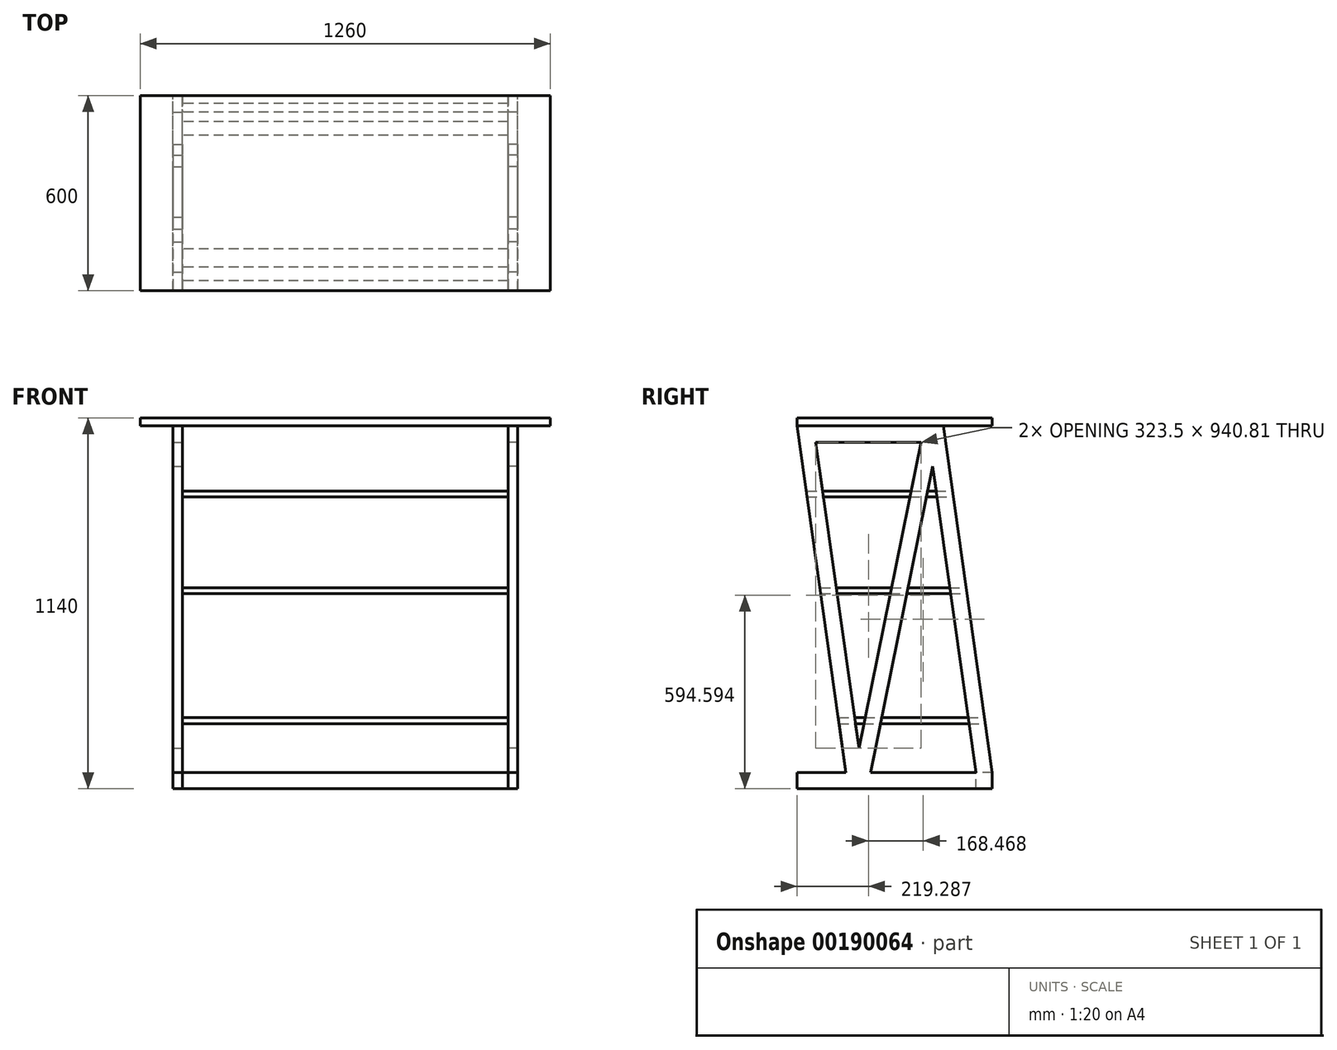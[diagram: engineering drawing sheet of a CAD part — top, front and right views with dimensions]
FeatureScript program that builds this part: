
annotation { "Feature Type Name" : "Feature", "Feature Type Description" : "" }
export const myFeature = defineFeature(function(context is Context, id is Id, definition is map)
    precondition{}
    {
        {
            var Q0;
            Q0=qCreatedBy(makeId("Right.planeOp"),FACE);
            cPlane(context, id + "F0", {"entities" : qUnion([Q0]), "cplaneType" : CPlaneType.OFFSET, "offset" : 500 * mm, "width" : 150 * mm, "height" : 150 * mm});
        }
        {
            var Q0;
            Q0=qCreatedBy(id+"F0.planeOp",FACE);
            var sketch = newSketch(context, id + "F1", { "sketchPlane" : qUnion([Q0])});
            skLineSegment(sketch, "E0", {"start": v(-600, 0) * mm, "end": v(0, 0) * mm});
            skLineSegment(sketch, "E1", {"start": v(-150, 1115) * mm, "end": v(-600, 1115) * mm});
            skLineSegment(sketch, "E2", {"start": v(-600, 1115) * mm, "end": v(-450, 50) * mm});
            skLineSegment(sketch, "E3", {"start": v(-542.46, 1065) * mm, "end": v(-409.96, 124.19) * mm});
            skLineSegment(sketch, "E4", {"start": v(-374, 50) * mm, "end": v(-50.5, 50) * mm});
            skLineSegment(sketch, "E5", {"start": v(-600, 1115) * mm, "end": v(-600, 0) * mm, "construction": true});
            skLineSegment(sketch, "E6", {"start": v(-600, 1115) * mm, "end": v(-600, 1115) * mm});
            skLineSegment(sketch, "E7", {"start": v(-600, 0) * mm, "end": v(-600, 50) * mm});
            skLineSegment(sketch, "E8", {"start": v(-600, 50) * mm, "end": v(-450, 50) * mm});
            skLineSegment(sketch, "E9", {"start": v(-150, 1115) * mm, "end": v(0, 1115) * mm, "construction": true});
            skLineSegment(sketch, "E10", {"start": v(-150, 1115) * mm, "end": v(0, 50) * mm});
            skLineSegment(sketch, "E11", {"start": v(0, 50) * mm, "end": v(0, 0) * mm});
            skLineSegment(sketch, "E12", {"start": v(0, 1115) * mm, "end": v(0, 50) * mm, "construction": true});
            skLineSegment(sketch, "E13", {"start": v(-542.46, 1065) * mm, "end": v(-218.96, 1065) * mm});
            skLineSegment(sketch, "E14", {"start": v(-183, 990.81) * mm, "end": v(-50.5, 50) * mm});
            skLineSegment(sketch, "E15", {"start": v(-193.45, 1065) * mm, "end": v(-399.5, 50) * mm, "construction": true});
            skLineSegment(sketch, "E16.0", {"start": v(-183, 990.81) * mm, "end": v(-374, 50) * mm});
            skLineSegment(sketch, "E17.0", {"start": v(-218.96, 1065) * mm, "end": v(-409.96, 124.19) * mm});
            skSolve(sketch);
        }
        {
            var Q0;
            Q0=qSketchRegion(id+"F1",true);
            extrude(context, id + "F2", {"entities" : qUnion([Q0]), "depth" : 30 * mm});
        }
        {
            var Q0;
            Q0=qCreatedBy(makeId("Front.planeOp"),FACE);
            var sketch = newSketch(context, id + "F3", { "sketchPlane" : qUnion([Q0])});
            skLineSegment(sketch, "E18.bottom", {"start": v(0, 1140) * mm, "end": v(630, 1140) * mm});
            skLineSegment(sketch, "E18.top", {"start": v(0, 1115) * mm, "end": v(630, 1115) * mm});
            skLineSegment(sketch, "E18.left", {"start": v(0, 1140) * mm, "end": v(0, 1115) * mm});
            skLineSegment(sketch, "E18.right", {"start": v(630, 1140) * mm, "end": v(630, 1115) * mm});
            skSolve(sketch);
        }
        {
            var Q0;
            Q0=qSketchRegion(id+"F3",true);
            extrude(context, id + "F4", {"entities" : qUnion([Q0]), "operationType" : NewBodyOperationType.ADD, "depth" : 600 * mm});
        }
        {
            var Q0;
            Q0=qCreatedBy(makeId("Right.planeOp"),FACE);
            var sketch = newSketch(context, id + "F5", { "sketchPlane" : qUnion([Q0])});
            skLineSegment(sketch, "E19.bottom", {"start": v(-569.3, 915) * mm, "end": v(-121.83, 915) * mm});
            skLineSegment(sketch, "E19.top", {"start": v(-569.3, 897) * mm, "end": v(-121.83, 897) * mm});
            skLineSegment(sketch, "E19.left", {"start": v(-569.3, 915) * mm, "end": v(-569.3, 897) * mm});
            skLineSegment(sketch, "E19.right", {"start": v(-121.83, 915) * mm, "end": v(-121.83, 897) * mm});
            skLineSegment(sketch, "E20.bottom", {"start": v(-527.46, 618) * mm, "end": v(-80, 618) * mm});
            skLineSegment(sketch, "E20.top", {"start": v(-527.46, 600) * mm, "end": v(-80, 600) * mm});
            skLineSegment(sketch, "E20.left", {"start": v(-527.46, 618) * mm, "end": v(-527.46, 600) * mm});
            skLineSegment(sketch, "E20.right", {"start": v(-80, 618) * mm, "end": v(-80, 600) * mm});
            skLineSegment(sketch, "E21.bottom", {"start": v(-471.13, 218) * mm, "end": v(-23.66, 218) * mm});
            skLineSegment(sketch, "E21.top", {"start": v(-471.13, 200) * mm, "end": v(-23.66, 200) * mm});
            skLineSegment(sketch, "E21.left", {"start": v(-471.13, 218) * mm, "end": v(-471.13, 200) * mm});
            skLineSegment(sketch, "E21.right", {"start": v(-23.66, 218) * mm, "end": v(-23.66, 200) * mm});
            skSolve(sketch);
        }
        {
            var Q0;
            Q0=qSketchRegion(id+"F5",true);
            var Q1;
            Q1=makeQuery(id+"F2.opExtrude","CAP_FACE",FACE,{"disambiguationData":[OSD([sQuery(id+"F1.wireOp",EDGE,"UNrtdt81-7Hrg-ewNu-V1ac-AiCCj1lCqIX2"),sQuery(id+"F1.wireOp",EDGE,"IiWHNMa0-QshA-bx21-GjYC-rvs6wlfJ4DpU"),sQuery(id+"F1.wireOp",EDGE,"6Mbc7M4e-MJ9J-6Adg-T8ZS-lolapjd4f5jQ"),sQuery(id+"F1.wireOp",EDGE,"mxtNMMIh-QTfc-XXiG-9IBl-Pp0JWCR6d1Oy"),sQuery(id+"F1.wireOp",EDGE,"E0"),sQuery(id+"F1.wireOp",EDGE,"zYNyOOiU-BwU6-h5NR-Uugv-CPKakWwIaoL4"),sQuery(id+"F1.wireOp",EDGE,"E1"),sQuery(id+"F1.wireOp",EDGE,"E2"),sQuery(id+"F1.wireOp",EDGE,"E3"),sQuery(id+"F1.wireOp",EDGE,"E4"),sQuery(id+"F1.wireOp",EDGE,"6OVXxlNC-ceYn-dU3p-YEhF-kSSgLO3tFiUR"),sQuery(id+"F1.wireOp",EDGE,"Am7mBALq-bMM0-lsHX-aXBU-YrHYZIsaEpz3")])],"isStart":true});
            extrude(context, id + "F6", {"entities" : qUnion([Q0]), "operationType" : NewBodyOperationType.ADD, "endBound" : BoundingType.UP_TO_SURFACE, "endBoundEntityFace" : qUnion([Q1]), "depth" : 25 * mm});
        }
        {
            var Q0;
            Q0=qCreatedBy(makeId("Right.planeOp"),FACE);
            var sketch = newSketch(context, id + "F7", { "sketchPlane" : qUnion([Q0])});
            skLineSegment(sketch, "E22.bottom", {"start": v(0, 0) * mm, "end": v(-50.5, 0) * mm});
            skLineSegment(sketch, "E22.top", {"start": v(0, 50) * mm, "end": v(-50.5, 50) * mm});
            skLineSegment(sketch, "E22.left", {"start": v(0, 0) * mm, "end": v(0, 50) * mm});
            skLineSegment(sketch, "E22.right", {"start": v(-50.5, 0) * mm, "end": v(-50.5, 50) * mm});
            skSolve(sketch);
        }
        {
            var Q0;
            Q0 = qSketchRegion(id + "F7", true);
            var Q1;
            {var subQ0=sQuery(id+"F1.wireOp",EDGE,"E11");var subQ1=sQuery(id+"F1.wireOp",EDGE,"E10");var subQ2=sQuery(id+"F1.wireOp",EDGE,"E7");var subQ3=sQuery(id+"F1.wireOp",EDGE,"E4");var subQ4=sQuery(id+"F1.wireOp",EDGE,"E0");var subQ5=sQuery(id+"F1.wireOp",EDGE,"E8");var subQ6=sQuery(id+"F1.wireOp",EDGE,"E14");var subQ7=sQuery(id+"F1.wireOp",EDGE,"E13");var subQ8=sQuery(id+"F1.wireOp",EDGE,"E3");var subQ9=sQuery(id+"F1.wireOp",EDGE,"E2");var subQ10=sQuery(id+"F1.wireOp",EDGE,"E1");var subQ11=makeQuery(id+"F2.opExtrude","CAP_FACE",FACE,{"disambiguationData":[OSD([subQ4,subQ10,subQ9,subQ8,subQ3,subQ2,subQ5,subQ1,subQ0,subQ7,subQ6])],"isStart":true});var subQ12=sQuery(id+"F5.wireOp",EDGE,"E21.bottom");var subQ13=sQuery(id+"F5.wireOp",EDGE,"E21.top");var subQ14=sQuery(id+"F5.wireOp",EDGE,"E21.left");var subQ15=sQuery(id+"F5.wireOp",EDGE,"E21.right");Q1=makeQuery(id+"F6.boolean.opBoolean","SPLIT",FACE,{"disambiguationData":[TD([makeQuery(id+"F2.opExtrude","SWEPT_FACE",FACE,{"disambiguationData":[OSD([subQ4])]}),subQ11,makeQuery(id+"F2.opExtrude","SWEPT_FACE",FACE,{"disambiguationData":[OSD([subQ9])]}),makeQuery(id+"F2.opExtrude","SWEPT_FACE",FACE,{"disambiguationData":[OSD([subQ8])]}),makeQuery(id+"F2.opExtrude","SWEPT_FACE",FACE,{"disambiguationData":[OSD([subQ3])]}),makeQuery(id+"F2.opExtrude","SWEPT_FACE",FACE,{"disambiguationData":[OSD([subQ2])]}),makeQuery(id+"F2.opExtrude","SWEPT_FACE",FACE,{"disambiguationData":[OSD([subQ5])]}),makeQuery(id+"F2.opExtrude","SWEPT_FACE",FACE,{"disambiguationData":[OSD([subQ1])]}),makeQuery(id+"F2.opExtrude","SWEPT_FACE",FACE,{"disambiguationData":[OSD([subQ0])]}),makeQuery(id+"F2.opExtrude","SWEPT_FACE",FACE,{"disambiguationData":[OSD([subQ6])]}),makeQuery(id+"F6.opExtrude","SWEPT_FACE",FACE,{"disambiguationData":[OSD([subQ12])]}),makeQuery(id+"F6.opExtrude","SWEPT_FACE",FACE,{"disambiguationData":[OSD([subQ13])]}),makeQuery(id+"F6.opExtrude","SWEPT_FACE",FACE,{"disambiguationData":[OSD([subQ14])]}),makeQuery(id+"F6.opExtrude","SWEPT_FACE",FACE,{"disambiguationData":[OSD([subQ15])]}),makeQuery(id+"F6.opExtrude","CAP_FACE",FACE,{"disambiguationData":[OSD([subQ4,subQ10,subQ9,subQ8,subQ3,subQ2,subQ5,subQ1,subQ0,subQ7,subQ6]),ownerDisambiguation([makeQuery(id+"F6.opExtrude","SWEPT_BODY",BODY,{"disambiguationData":[OSD([subQ12,subQ13,subQ14,subQ15])]})])],"isStart":false})])],"derivedFrom":subQ11});}
            extrude(context, id + "F8", {"entities" : qUnion([Q0]), "operationType" : NewBodyOperationType.ADD, "endBound" : BoundingType.UP_TO_SURFACE, "endBoundEntityFace" : qUnion([Q1]), "depth" : 25 * mm});
        }
        {
            var Q0;
            Q0=makeQuery(id+"F2.opExtrude","SWEPT_BODY",BODY,{"disambiguationData":[OSD([sQuery(id+"F1.wireOp",EDGE,"UNrtdt81-7Hrg-ewNu-V1ac-AiCCj1lCqIX2"),sQuery(id+"F1.wireOp",EDGE,"IiWHNMa0-QshA-bx21-GjYC-rvs6wlfJ4DpU"),sQuery(id+"F1.wireOp",EDGE,"6Mbc7M4e-MJ9J-6Adg-T8ZS-lolapjd4f5jQ"),sQuery(id+"F1.wireOp",EDGE,"mxtNMMIh-QTfc-XXiG-9IBl-Pp0JWCR6d1Oy"),sQuery(id+"F1.wireOp",EDGE,"E0"),sQuery(id+"F1.wireOp",EDGE,"zYNyOOiU-BwU6-h5NR-Uugv-CPKakWwIaoL4"),sQuery(id+"F1.wireOp",EDGE,"E1"),sQuery(id+"F1.wireOp",EDGE,"E2"),sQuery(id+"F1.wireOp",EDGE,"E3"),sQuery(id+"F1.wireOp",EDGE,"E4"),sQuery(id+"F1.wireOp",EDGE,"6OVXxlNC-ceYn-dU3p-YEhF-kSSgLO3tFiUR"),sQuery(id+"F1.wireOp",EDGE,"Am7mBALq-bMM0-lsHX-aXBU-YrHYZIsaEpz3")])]});
            var Q1;
            Q1=qCreatedBy(makeId("Right.planeOp"),FACE);
            mirror(context, id + "F9", {"operationType" : NewBodyOperationType.ADD, "entities" : qUnion([Q0]), "mirrorPlane" : qUnion([Q1])});
        }
    });
